# Revit family: Elevator_Accessories_Garaventa_ControlUnit
name_source: partatom
category: Generic Models
units: mm (PartAtom-declared; Revit-internal decimal feet)

## family parameters
Always vertical = No
Can host rebar = No
Classification Number = 23.50.05.11.24.14
Cut with Voids When Loaded = No
Maintain Annotation Orientation = No
Part Type = Normal
Room Calculation Point = No
Round Connector Dimension = Use Diameter
Shared = No
Work Plane-Based = Yes

## types (2) — shared parameters
Assembly Code = D1010
Construction Details = http://www.arcat.com
Default Elevation = 0' - 0"
Green Building-LEED = http://www.arcat.com
Keynote = 14 20 00
Manufacturer = Garaventa Lift
Manufacturer Fax = 604-594-9915
Manufacturer Website = http://www.garaventalift.com
Product Data = http://www.arcat.com
Revision = R1_2017-06
Sales Information = http://www.garaventalift.com
SpecWizard = http://www.arcat.com
Specification = http://www.arcat.com
URL = http://www.garaventalift.com
zero-valued in all types: Expected Lifespan (Years), Maintenance Schedule (Months), Warranty Duration (Years)

## per-type parameters (varying)
| type | Description | Inline Cabinet | Model | Unit Depth | Unit Height | Unit Width |
| InLine Cabinet | Garaventa Lift InLine Electric Elevator Control Cabinet | Yes | InLine | 0' - 10" | 1' - 6" | 1' - 8" |
| Hydraulic Cabinet | Garaventa Lift Hydraulic Elevator Control Cabinet | No | Hydraulic | 0' - 6" | 2' - 6" | 1' - 11" |

type visibility flags (boolean, named after types; folded from table):
- InLine Cabinet: Yes: (none)
- Hydraulic Cabinet: Yes: Hydraulic Cabinet

## geometry (parser evidence)
native form markers: Sweep x2
no freeform markers — native parametric forms only
